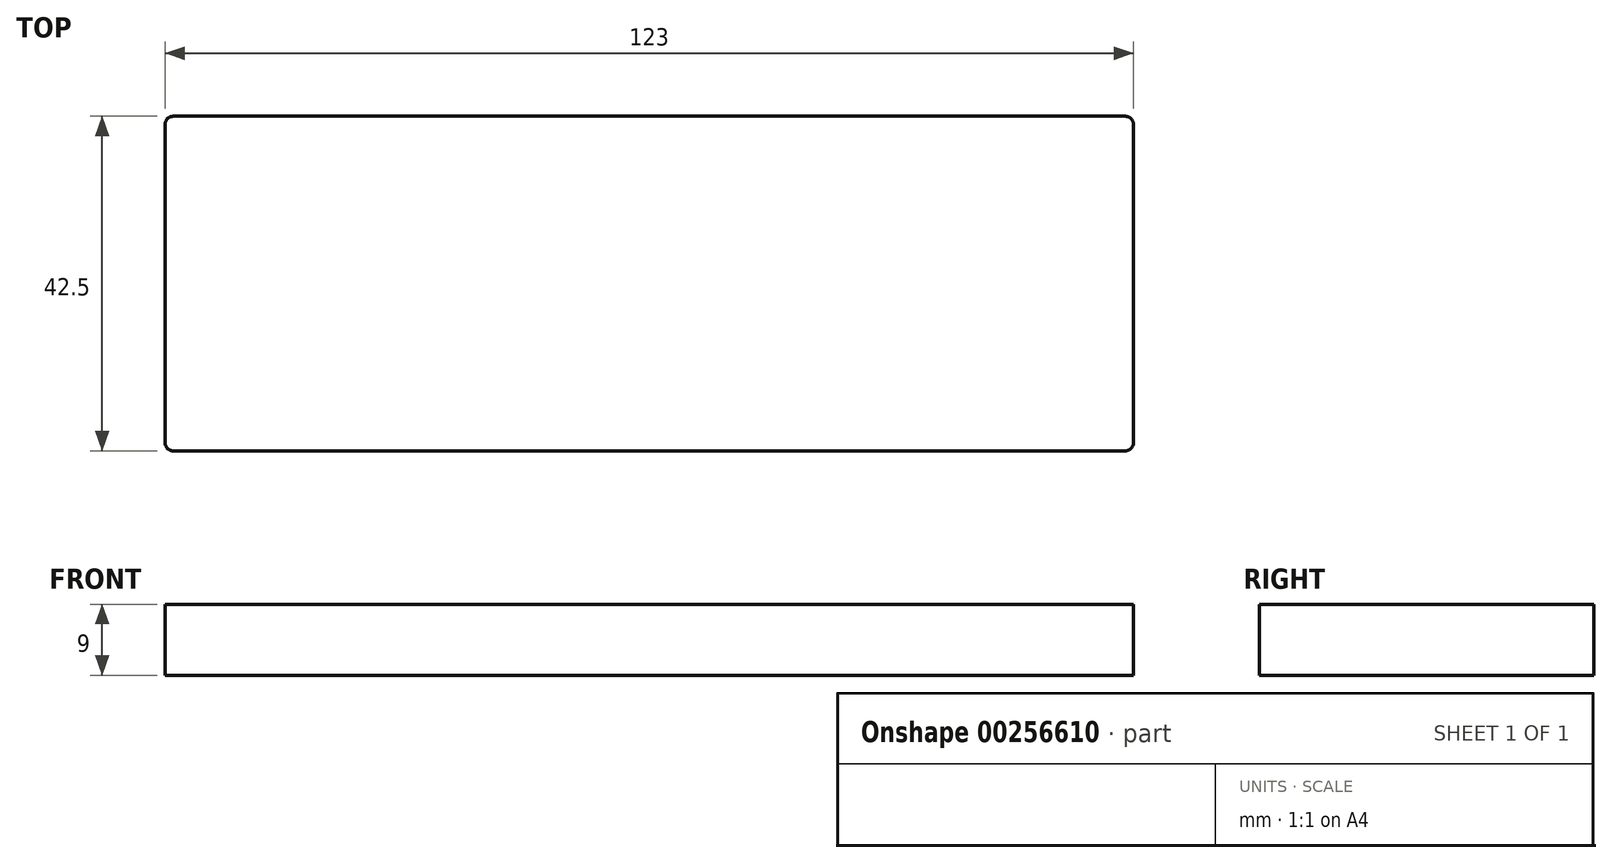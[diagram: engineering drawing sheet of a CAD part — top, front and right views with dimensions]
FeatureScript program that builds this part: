
annotation { "Feature Type Name" : "Feature", "Feature Type Description" : "" }
export const myFeature = defineFeature(function(context is Context, id is Id, definition is map)
    precondition{}
    {
        {
            var Q0;
            Q0=qCreatedBy(makeId("Top.planeOp"),FACE);
            var sketch = newSketch(context, id + "F0", { "sketchPlane" : qUnion([Q0])});
            skLineSegment(sketch, "E0.bottom", {"start": v(60.5, -21.25) * mm, "end": v(-60.5, -21.25) * mm});
            skLineSegment(sketch, "E0.top", {"start": v(60.5, 21.25) * mm, "end": v(-60.5, 21.25) * mm});
            skLineSegment(sketch, "E0.left", {"start": v(61.5, -20.25) * mm, "end": v(61.5, 20.25) * mm});
            skLineSegment(sketch, "E0.right", {"start": v(-61.5, -20.25) * mm, "end": v(-61.5, 20.25) * mm});
            skPoint(sketch, "E0.middle", {"position": v(0, 0) * mm});
            skPoint(sketch, "E1.visualSharp", {"position": v(-61.5, 21.25) * mm});
            skArc(sketch, "E1.filletArc", {"start": v(-60.5, 21.25) * mm, "mid": v(-61.2, 20.96) * mm, "end": v(-61.5, 20.25) * mm});
            skPoint(sketch, "E2.visualSharp", {"position": v(-61.5, -21.25) * mm});
            skArc(sketch, "E2.filletArc", {"start": v(-61.5, -20.25) * mm, "mid": v(-61.2, -20.96) * mm, "end": v(-60.5, -21.25) * mm});
            skPoint(sketch, "E3.visualSharp", {"position": v(61.5, 21.25) * mm});
            skArc(sketch, "E3.filletArc", {"start": v(61.5, 20.25) * mm, "mid": v(61.2, 20.96) * mm, "end": v(60.5, 21.25) * mm});
            skPoint(sketch, "E4.visualSharp", {"position": v(61.5, -21.25) * mm});
            skArc(sketch, "E4.filletArc", {"start": v(60.5, -21.25) * mm, "mid": v(61.2, -20.96) * mm, "end": v(61.5, -20.25) * mm});
            skSolve(sketch);
        }
        {
            var Q0;
            Q0=makeQuery(id+"F0.imprint","IMPRINT",FACE,{"disambiguationData":[TD([[makeQuery(id+"F0.imprint","IMPRINT",EDGE,{"derivedFrom":sQuery(id+"F0.wireOp",EDGE,"E0.bottom")}),-1.0]])]});
            extrude(context, id + "F1", {"entities" : qUnion([Q0]), "depth" : 9 * mm});
        }
    });
